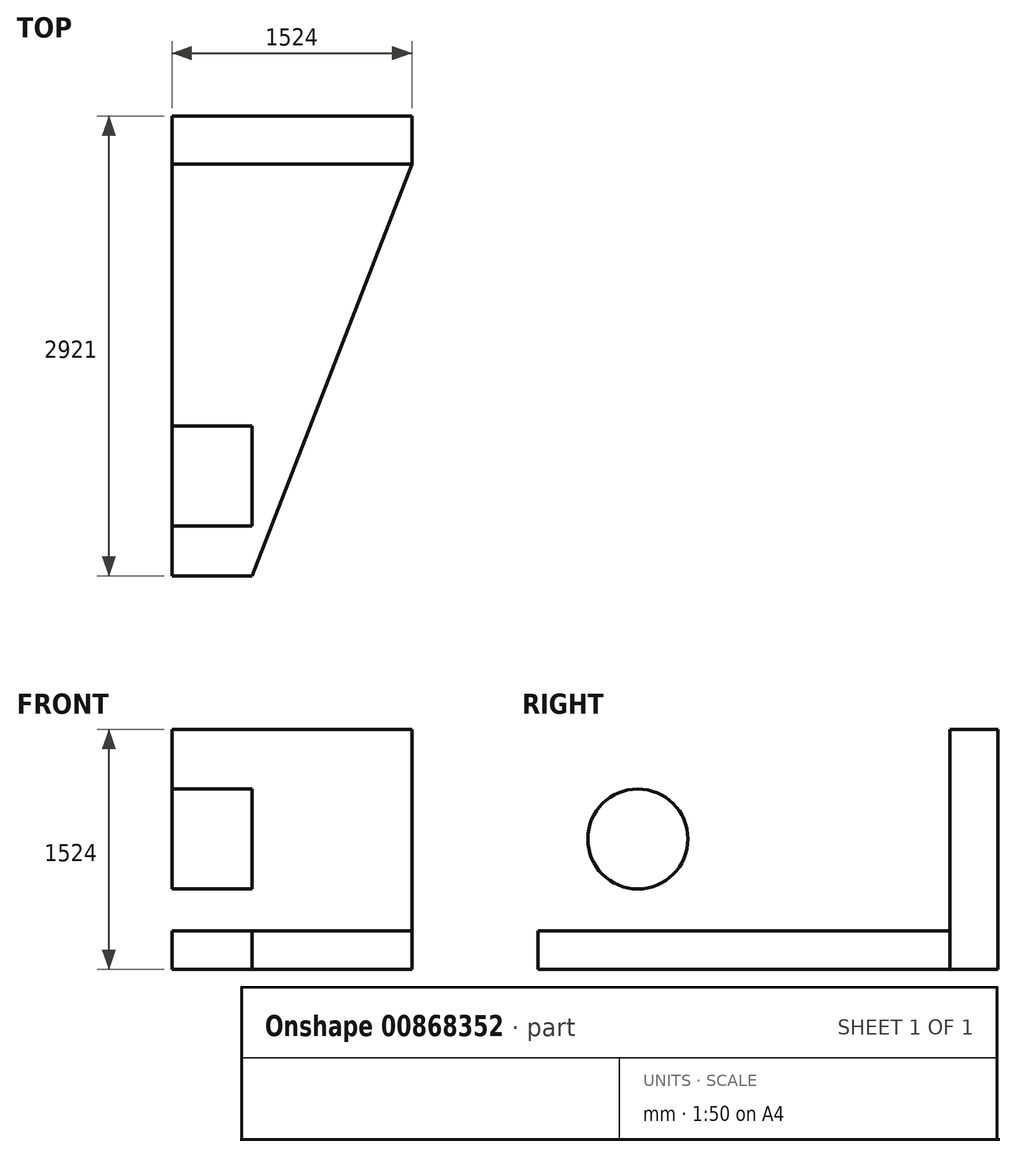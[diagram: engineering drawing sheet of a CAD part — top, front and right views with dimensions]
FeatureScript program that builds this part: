
annotation { "Feature Type Name" : "Feature", "Feature Type Description" : "" }
export const myFeature = defineFeature(function(context is Context, id is Id, definition is map)
    precondition{}
    {
        {
            var Q0;
            Q0=qCreatedBy(makeId("Front.planeOp"),FACE);
            var sketch = newSketch(context, id + "F0", { "sketchPlane" : qUnion([Q0])});
            skLineSegment(sketch, "E0.bottom", {"start": v(0, 0) * mm, "end": v(-1524, 0) * mm});
            skLineSegment(sketch, "E0.top", {"start": v(0, 1524) * mm, "end": v(-1524, 1524) * mm});
            skLineSegment(sketch, "E0.left", {"start": v(0, 0) * mm, "end": v(0, 1524) * mm});
            skLineSegment(sketch, "E0.right", {"start": v(-1524, 0) * mm, "end": v(-1524, 1524) * mm});
            skSolve(sketch);
        }
        {
            var Q0;
            Q0 = qSketchRegion(id + "F0", true);
            extrude(context, id + "F1", {"entities" : qUnion([Q0]), "depth" : 304.8 * mm, "offsetDistance" : 25.4 * mm});
        }
        {
            var Q0;
            Q0=makeQuery(id+"F1.opExtrude","CAP_FACE",FACE,{"disambiguationData":[OSD([sQuery(id+"F0.wireOp",EDGE,"E0.bottom"),sQuery(id+"F0.wireOp",EDGE,"E0.top"),sQuery(id+"F0.wireOp",EDGE,"E0.left"),sQuery(id+"F0.wireOp",EDGE,"E0.right")])],"isStart":false});
            var sketch = newSketch(context, id + "F2", { "sketchPlane" : qUnion([Q0])});
            skLineSegment(sketch, "E1.bottom", {"start": v(-1524, 0) * mm, "end": v(0, 0) * mm});
            skLineSegment(sketch, "E1.top", {"start": v(-1524, 244.35) * mm, "end": v(0, 244.35) * mm});
            skLineSegment(sketch, "E1.left", {"start": v(-1524, 0) * mm, "end": v(-1524, 244.35) * mm});
            skLineSegment(sketch, "E1.right", {"start": v(0, 0) * mm, "end": v(0, 244.35) * mm});
            skSolve(sketch);
        }
        {
            var Q0;
            Q0 = qSketchRegion(id + "F2", true);
            extrude(context, id + "F3", {"entities" : qUnion([Q0]), "operationType" : NewBodyOperationType.ADD, "depth" : 2616.2 * mm, "offsetDistance" : 25.4 * mm});
        }
        {
            var Q0;
            Q0=makeQuery(id+"F3.opExtrude","SWEPT_FACE",FACE,{"disambiguationData":[OSD([sQuery(id+"F2.wireOp",EDGE,"E1.top")])]});
            var sketch = newSketch(context, id + "F4", { "sketchPlane" : qUnion([Q0])});
            skLineSegment(sketch, "E2.bottom", {"start": v(-1524, -2921) * mm, "end": v(-1016, -2921) * mm});
            skLineSegment(sketch, "E2.top", {"start": v(-1524, -1651) * mm, "end": v(-1016, -1651) * mm});
            skLineSegment(sketch, "E2.left", {"start": v(-1524, -2921) * mm, "end": v(-1524, -1651) * mm});
            skLineSegment(sketch, "E2.right", {"start": v(-1016, -2921) * mm, "end": v(-1016, -1651) * mm});
            skSolve(sketch);
        }
        {
            var Q0;
            Q0 = qSketchRegion(id + "F4", true);
            extrude(context, id + "F5", {"entities" : qUnion([Q0]), "operationType" : NewBodyOperationType.ADD, "depth" : 584.2 * mm, "offsetDistance" : 25.4 * mm});
        }
        {
            var Q0;
            Q0=makeQuery(id+"F5.opExtrude","SWEPT_FACE",FACE,{"disambiguationData":[OSD([sQuery(id+"F4.wireOp",EDGE,"E2.right")])]});
            var sketch = newSketch(context, id + "F6", { "sketchPlane" : qUnion([Q0])});
            skCircle(sketch, "E3", {"center": v(-2286, 828.55) * mm, "radius": 635 * mm});
            skSolve(sketch);
        }
        {
            var Q0;
            {var subQ1=sQuery(id+"F4.wireOp",EDGE,"E2.right");var subQ2=makeQuery(id+"F5.opExtrude","CAP_EDGE",EDGE,{"disambiguationData":[OSD([subQ1])],"isStart":false});Q0=makeQuery(id+"F6.imprint","IMPRINT",FACE,{"disambiguationData":[TD([[makeQuery(id+"F6.imprint","IMPRINT",EDGE,{"derivedFrom":subQ2}),1.0]])]});}
            var Q1;
            {var subQ0=sQuery(id+"F6.wireOp",EDGE,"E3");var subQ1=makeQuery(id+"F5.opExtrude","CAP_EDGE",EDGE,{"disambiguationData":[OSD([sQuery(id+"F4.wireOp",EDGE,"E2.right")])],"isStart":true});var subQ2=makeQuery(id+"F6.imprint","INTERSECT",VERTEX,{"disambiguationData":[OD(0.0)],"derivedFrom":[subQ1,subQ0]});Q1=makeQuery(id+"F6.imprint","IMPRINT",FACE,{"disambiguationData":[TD([[makeQuery(id+"F6.imprint","IMPRINT",EDGE,{"disambiguationData":[TD([[subQ2,-1.0]])],"derivedFrom":subQ0}),1.0]])]});}
            extrude(context, id + "F7", {"entities" : qUnion([Q0, Q1]), "operationType" : NewBodyOperationType.ADD, "oppositeDirection" : true, "depth" : 508 * mm, "offsetDistance" : 25.4 * mm});
        }
        {
            var Q0;
            {var subQ0=sQuery(id+"F4.wireOp",EDGE,"E2.right");var subQ1=makeQuery(id+"F5.opExtrude","CAP_EDGE",EDGE,{"disambiguationData":[OSD([subQ0])],"isStart":false});var subQ2=sQuery(id+"F6.wireOp",EDGE,"E3");Q0=makeQuery(id+"F7.boolean.opBoolean","MERGE",FACE,{"derivedFrom":[makeQuery(id+"F5.opExtrude","SWEPT_FACE",FACE,{"disambiguationData":[OSD([subQ0])]}),makeQuery(id+"F7.opExtrude","CAP_FACE",FACE,{"disambiguationData":[OSD([subQ0,subQ2]),TDD([makeQuery(id+"F6.imprint","IMPRINT",EDGE,{"disambiguationData":[TD([[makeQuery(id+"F6.imprint","INTERSECT",VERTEX,{"derivedFrom":[makeQuery(id+"F5.opExtrude","SWEPT_EDGE",EDGE,{"disambiguationData":[OSD([sQuery(id+"F4.wireOp",EDGE,"E2.top"),subQ0])]}),subQ1,subQ2]}),-1.0]])],"derivedFrom":subQ2}),makeQuery(id+"F6.imprint","IMPRINT",EDGE,{"derivedFrom":subQ1})])],"isStart":true})]});}
            var sketch = newSketch(context, id + "F8", { "sketchPlane" : qUnion([Q0])});
            skLineSegment(sketch, "E4", {"start": v(-2921, 828.55) * mm, "end": v(-1651, 828.55) * mm});
            skCircle(sketch, "E5", {"center": v(-2286, 828.55) * mm, "radius": 317.5 * mm});
            skSolve(sketch);
        }
        {
            var Q0;
            {var subQ0=sQuery(id+"F8.wireOp",EDGE,"E5");var subQ1=sQuery(id+"F8.wireOp",EDGE,"E4");var subQ2=makeQuery(id+"F8.imprint","INTERSECT",VERTEX,{"disambiguationData":[OD(0.0)],"derivedFrom":[subQ1,subQ0]});Q0=makeQuery(id+"F8.imprint","IMPRINT",FACE,{"disambiguationData":[TD([[makeQuery(id+"F8.imprint","IMPRINT",EDGE,{"disambiguationData":[TD([[subQ2,-1.0]])],"derivedFrom":subQ1}),1.0]])]});}
            var Q1;
            {var subQ0=sQuery(id+"F8.wireOp",EDGE,"E5");var subQ1=sQuery(id+"F8.wireOp",EDGE,"E4");var subQ2=makeQuery(id+"F8.imprint","INTERSECT",VERTEX,{"disambiguationData":[OD(0.0)],"derivedFrom":[subQ1,subQ0]});Q1=makeQuery(id+"F8.imprint","IMPRINT",FACE,{"disambiguationData":[TD([[makeQuery(id+"F8.imprint","IMPRINT",EDGE,{"disambiguationData":[TD([[subQ2,-1.0]])],"derivedFrom":subQ1}),-1.0]])]});}
            extrude(context, id + "F9", {"entities" : qUnion([Q0, Q1]), "operationType" : NewBodyOperationType.REMOVE, "oppositeDirection" : true, "depth" : 508 * mm, "offsetDistance" : 25.4 * mm});
        }
        {
            var Q0;
            Q0=makeQuery(id+"F3.opExtrude","SWEPT_FACE",FACE,{"disambiguationData":[OSD([sQuery(id+"F2.wireOp",EDGE,"E1.top")])]});
            var sketch = newSketch(context, id + "F10", { "sketchPlane" : qUnion([Q0])});
            skLineSegment(sketch, "E6", {"start": v(-1016, -2921) * mm, "end": v(0, -304.8) * mm});
            skSolve(sketch);
        }
        {
            var Q0;
            Q0 = qSketchRegion(id + "F10", true);
            var Q1;
            Q1=makeQuery(id+"F10.imprint","IMPRINT",FACE,{"disambiguationData":[TD([[makeQuery(id+"F10.imprint","IMPRINT",EDGE,{"derivedFrom":sQuery(id+"F10.wireOp",EDGE,"E6")}),-1.0]])]});
            extrude(context, id + "F11", {"entities" : qUnion([Q0, Q1]), "operationType" : NewBodyOperationType.REMOVE, "oppositeDirection" : true, "depth" : 304.8 * mm, "offsetDistance" : 25.4 * mm});
        }
    });
